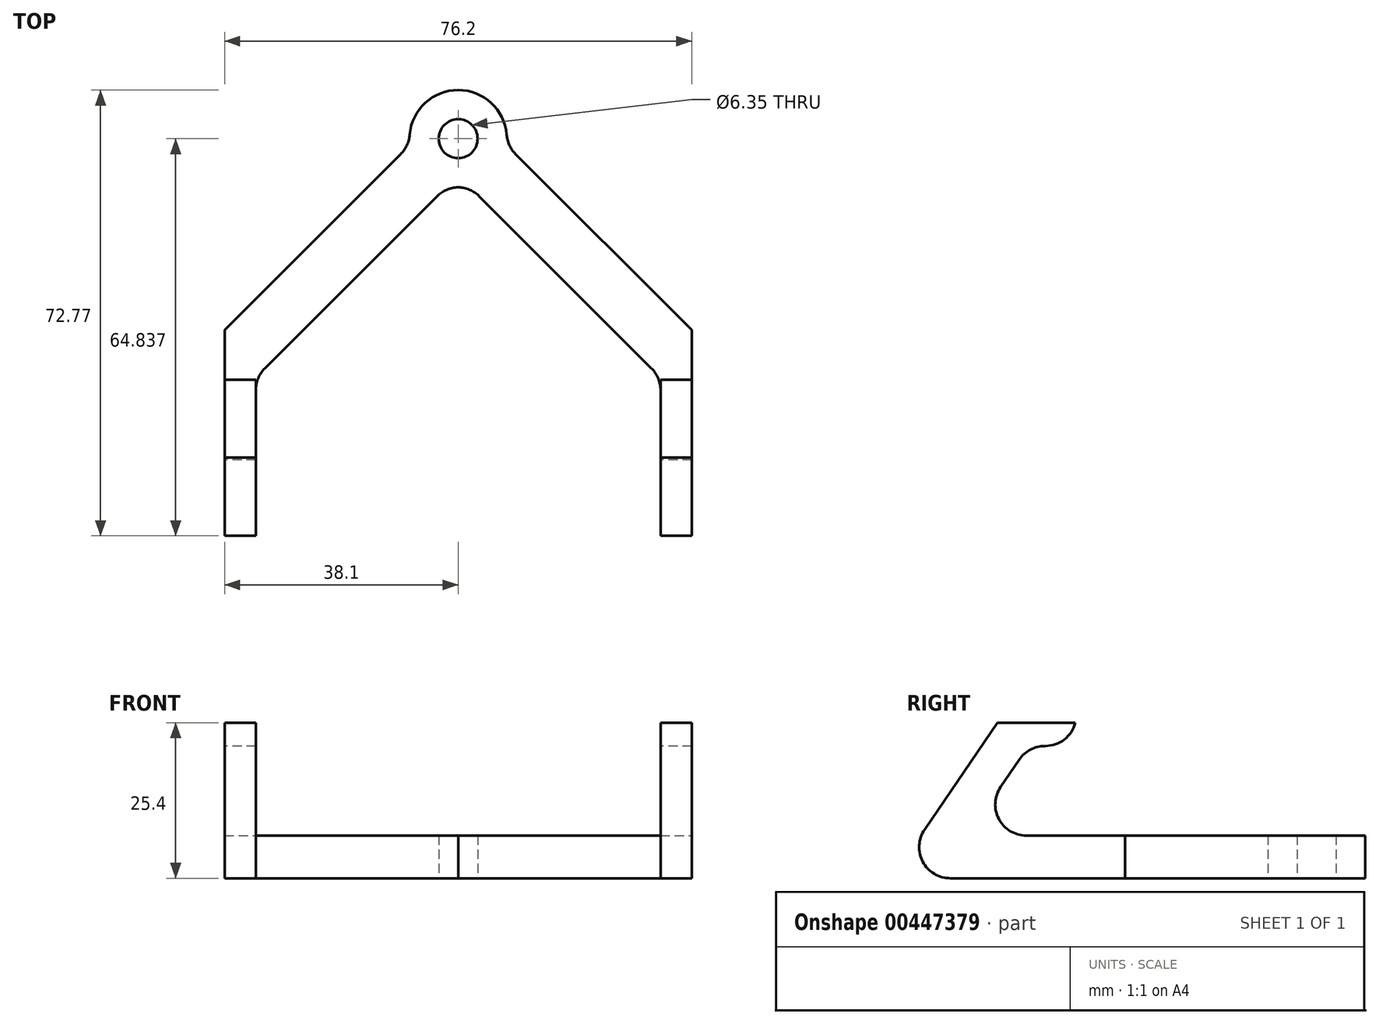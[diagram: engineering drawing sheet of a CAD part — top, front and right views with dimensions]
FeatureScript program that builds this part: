
annotation { "Feature Type Name" : "Feature", "Feature Type Description" : "" }
export const myFeature = defineFeature(function(context is Context, id is Id, definition is map)
    precondition{}
    {
        {
            var Q0;
            Q0=qCreatedBy(makeId("Top.planeOp"),FACE);
            var sketch = newSketch(context, id + "F0", { "sketchPlane" : qUnion([Q0])});
            skLineSegment(sketch, "E0.bottom", {"start": v(38.1, -38.1) * mm, "end": v(-38.1, -38.1) * mm});
            skLineSegment(sketch, "E0.top", {"start": v(38.1, 38.1) * mm, "end": v(-38.1, 38.1) * mm});
            skLineSegment(sketch, "E0.left", {"start": v(38.1, -38.1) * mm, "end": v(38.1, 38.1) * mm});
            skLineSegment(sketch, "E0.right", {"start": v(-38.1, -38.1) * mm, "end": v(-38.1, 38.1) * mm});
            skPoint(sketch, "E0.middle", {"position": v(0, 0) * mm});
            skSolve(sketch);
        }
        {
            var Q0;
            Q0=makeQuery(id+"F0.imprint","IMPRINT",FACE,{"disambiguationData":[TD([[makeQuery(id+"F0.imprint","IMPRINT",EDGE,{"derivedFrom":sQuery(id+"F0.wireOp",EDGE,"E0.bottom")}),-1.0]])]});
            extrude(context, id + "F1", {"entities" : qUnion([Q0]), "depth" : 25.4 * mm});
        }
        {
            var Q0;
            Q0=qCreatedBy(makeId("Right.planeOp"),FACE);
            var sketch = newSketch(context, id + "F2", { "sketchPlane" : qUnion([Q0])});
            skLineSegment(sketch, "E1.0.1", {"start": v(-38.1, 0) * mm, "end": v(-38.1, 25.4) * mm});
            skLineSegment(sketch, "E1.0.2", {"start": v(-38.1, 25.4) * mm, "end": v(-20.84, 25.4) * mm});
            skLineSegment(sketch, "E1.0.3", {"start": v(38.1, 25.4) * mm, "end": v(38.1, 6.96) * mm});
            skLineSegment(sketch, "E2", {"start": v(-8.1, 25.4) * mm, "end": v(-8.1, 21.59) * mm});
            skLineSegment(sketch, "E3", {"start": v(-8.1, 21.59) * mm, "end": v(-15.75, 21.59) * mm});
            skLineSegment(sketch, "E4", {"start": v(-15.75, 21.6) * mm, "end": v(-25.7, 6.96) * mm});
            skPoint(sketch, "E5.orphan", {"position": v(-30.42, 0) * mm});
            skLineSegment(sketch, "E6", {"start": v(-25.7, 6.96) * mm, "end": v(38.1, 6.96) * mm});
            skLineSegment(sketch, "E7", {"start": v(-20.84, 25.4) * mm, "end": v(-38.1, 0) * mm});
            skPoint(sketch, "E8.orphan", {"position": v(38.1, 0) * mm});
            skLineSegment(sketch, "E9.trimOffspring", {"start": v(-8.1, 25.4) * mm, "end": v(38.1, 25.4) * mm});
            skSolve(sketch);
        }
        {
            var Q0;
            Q0 = qSketchRegion(id + "F2", true);
            extrude(context, id + "F3", {"entities" : qUnion([Q0]), "operationType" : NewBodyOperationType.REMOVE, "endBound" : BoundingType.SYMMETRIC, "oppositeDirection" : true, "depth" : 76.2 * mm});
        }
        {
            var Q0;
            Q0=qCreatedBy(makeId("Top.planeOp"),FACE);
            var sketch = newSketch(context, id + "F4", { "sketchPlane" : qUnion([Q0])});
            skLineSegment(sketch, "E10.0.0", {"start": v(38.1, 0) * mm, "end": v(38.1, 38.1) * mm});
            skLineSegment(sketch, "E10.0.1", {"start": v(38.1, 38.1) * mm, "end": v(-38.1, 38.1) * mm});
            skLineSegment(sketch, "E10.0.2", {"start": v(-38.1, 38.1) * mm, "end": v(-38.1, 0) * mm});
            skLineSegment(sketch, "E10.0.3", {"start": v(-33.02, -38.1) * mm, "end": v(33.02, -38.1) * mm});
            skLineSegment(sketch, "E11.0.1", {"start": v(38.1, 38.1) * mm, "end": v(0, 38.1) * mm});
            skLineSegment(sketch, "E12", {"start": v(33.02, -38.1) * mm, "end": v(33.02, -7.73) * mm});
            skLineSegment(sketch, "E13", {"start": v(33.02, -7.73) * mm, "end": v(0, 25.3) * mm});
            skLineSegment(sketch, "E14", {"start": v(38.1, 0) * mm, "end": v(0, 38.1) * mm});
            skLineSegment(sketch, "E15.MirrorCS", {"start": v(-38.1, 0) * mm, "end": v(-38.1, 38.1) * mm});
            skLineSegment(sketch, "E16.MirrorCS", {"start": v(-33.02, -38.1) * mm, "end": v(-33.02, -7.73) * mm});
            skLineSegment(sketch, "E17.MirrorCS", {"start": v(-33.02, -7.73) * mm, "end": v(0, 25.3) * mm});
            skLineSegment(sketch, "E18.MirrorCS", {"start": v(-38.1, 0) * mm, "end": v(0, 38.1) * mm});
            skLineSegment(sketch, "E19", {"start": v(33.02, -38.1) * mm, "end": v(-33.02, -38.1) * mm});
            skPoint(sketch, "E20.orphan", {"position": v(38.1, -38.1) * mm});
            skPoint(sketch, "E21.orphan", {"position": v(-38.1, -38.1) * mm});
            skSolve(sketch);
        }
        {
            var Q0;
            Q0 = qSketchRegion(id + "F4", true);
            extrude(context, id + "F5", {"entities" : qUnion([Q0]), "operationType" : NewBodyOperationType.REMOVE, "endBound" : BoundingType.THROUGH_ALL, "depth" : 25.4 * mm});
        }
        {
            var Q0;
            Q0=makeQuery(id+"F0.imprint","IMPRINT",FACE,{"disambiguationData":[TD([[makeQuery(id+"F0.imprint","IMPRINT",EDGE,{"derivedFrom":sQuery(id+"F0.wireOp",EDGE,"E0.bottom")}),-1.0]])]});
            var sketch = newSketch(context, id + "F6", { "sketchPlane" : qUnion([Q0])});
            skCircle(sketch, "E22", {"center": v(0, 31.25) * mm, "radius": 7.94 * mm});
            skCircle(sketch, "E23", {"center": v(0, 31.25) * mm, "radius": 3.18 * mm});
            skSolve(sketch);
        }
        {
            var Q0;
            Q0=makeQuery(id+"F6.imprint","IMPRINT",FACE,{"disambiguationData":[TD([[makeQuery(id+"F6.imprint","IMPRINT",EDGE,{"derivedFrom":sQuery(id+"F6.wireOp",EDGE,"E23")}),-1.0]])]});
            var Q1;
            {var subQ0=sQuery(id+"F6.wireOp",EDGE,"E22");var subQ1=makeQuery(id+"F0.imprint","IMPRINT",EDGE,{"derivedFrom":sQuery(id+"F0.wireOp",EDGE,"E0.top")});var subQ2=makeQuery(id+"F6.imprint","INTERSECT",VERTEX,{"disambiguationData":[OD(0.0)],"derivedFrom":[subQ1,subQ0]});Q1=makeQuery(id+"F6.imprint","IMPRINT",FACE,{"disambiguationData":[TD([[makeQuery(id+"F6.imprint","IMPRINT",EDGE,{"disambiguationData":[TD([[subQ2,-1.0]])],"derivedFrom":subQ0}),1.0]])]});}
            var Q2;
            Q2=makeQuery(id+"F3.boolean.opBoolean","COPY",FACE,{"derivedFrom":makeQuery(id+"F3.opExtrude","SWEPT_FACE",FACE,{"disambiguationData":[OSD([sQuery(id+"F2.wireOp",EDGE,"E6")])]})});
            extrude(context, id + "F7", {"entities" : qUnion([Q0, Q1]), "operationType" : NewBodyOperationType.ADD, "endBound" : BoundingType.UP_TO_SURFACE, "endBoundEntityFace" : qUnion([Q2]), "depth" : 25.4 * mm});
        }
        {
            var Q0;
            Q0=makeQuery(id+"F6.imprint","IMPRINT",FACE,{"disambiguationData":[TD([[makeQuery(id+"F6.imprint","IMPRINT",EDGE,{"derivedFrom":sQuery(id+"F6.wireOp",EDGE,"E23")}),1.0]])]});
            extrude(context, id + "F8", {"entities" : qUnion([Q0]), "operationType" : NewBodyOperationType.REMOVE, "depth" : 25.4 * mm});
        }
        {
            var Q0;
            {var subQ0=sQuery(id+"F2.wireOp",EDGE,"E4");var subQ1=sQuery(id+"F2.wireOp",EDGE,"E6");Q0=makeQuery(id+"F5.boolean.opBoolean","SPLIT",EDGE,{"disambiguationData":[TD([makeQuery(id+"F1.opExtrude","SWEPT_FACE",FACE,{"disambiguationData":[OSD([sQuery(id+"F0.wireOp",EDGE,"E0.right")])]})])],"derivedFrom":makeQuery(id+"F3.boolean.opBoolean","COPY",EDGE,{"derivedFrom":makeQuery(id+"F3.opExtrude","SWEPT_EDGE",EDGE,{"disambiguationData":[OSD([subQ0,subQ1])]})})});}
            var Q1;
            Q1=makeQuery(id+"F5.boolean.opBoolean","COPY",EDGE,{"derivedFrom":makeQuery(id+"F5.opExtrude","SWEPT_EDGE",EDGE,{"disambiguationData":[OSD([sQuery(id+"F4.wireOp",EDGE,"E16.MirrorCS"),sQuery(id+"F4.wireOp",EDGE,"E17.MirrorCS")])]})});
            var Q2;
            Q2=makeQuery(id+"F5.boolean.opBoolean","COPY",EDGE,{"derivedFrom":makeQuery(id+"F5.opExtrude","SWEPT_EDGE",EDGE,{"disambiguationData":[OSD([sQuery(id+"F4.wireOp",EDGE,"E15.MirrorCS"),sQuery(id+"F4.wireOp",EDGE,"E18.MirrorCS")])]})});
            var Q3;
            Q3=makeQuery(id+"F5.boolean.opBoolean","COPY",EDGE,{"derivedFrom":makeQuery(id+"F5.opExtrude","SWEPT_EDGE",EDGE,{"disambiguationData":[OSD([sQuery(id+"F4.wireOp",EDGE,"E12"),sQuery(id+"F4.wireOp",EDGE,"E13")])]})});
            var Q4;
            Q4=makeQuery(id+"F5.boolean.opBoolean","COPY",EDGE,{"derivedFrom":makeQuery(id+"F5.opExtrude","SWEPT_EDGE",EDGE,{"disambiguationData":[OSD([sQuery(id+"F4.wireOp",EDGE,"E10.0.0"),sQuery(id+"F4.wireOp",EDGE,"E14")])]})});
            var Q5;
            {var subQ0=sQuery(id+"F2.wireOp",EDGE,"E4");var subQ1=sQuery(id+"F2.wireOp",EDGE,"E6");Q5=makeQuery(id+"F5.boolean.opBoolean","SPLIT",EDGE,{"disambiguationData":[TD([makeQuery(id+"F1.opExtrude","SWEPT_FACE",FACE,{"disambiguationData":[OSD([sQuery(id+"F0.wireOp",EDGE,"E0.left")])]})])],"derivedFrom":makeQuery(id+"F3.boolean.opBoolean","COPY",EDGE,{"derivedFrom":makeQuery(id+"F3.opExtrude","SWEPT_EDGE",EDGE,{"disambiguationData":[OSD([subQ0,subQ1])]})})});}
            fillet(context, id + "F9", {"entities" : qUnion([Q0, Q1, Q2, Q3, Q4, Q5]), "radius" : 5.08 * mm, "tangentPropagation" : true, "allowEdgeOverflow" : false});
        }
        {
            var Q0;
            {var subQ0=sQuery(id+"F0.wireOp",EDGE,"E0.left");var subQ1=sQuery(id+"F0.wireOp",EDGE,"E0.bottom");var subQ2=sQuery(id+"F2.wireOp",EDGE,"E7");Q0=makeQuery(id+"F5.boolean.opBoolean","SPLIT",EDGE,{"disambiguationData":[TD([makeQuery(id+"F1.opExtrude","SWEPT_FACE",FACE,{"disambiguationData":[OSD([subQ0])]})])],"derivedFrom":makeQuery(id+"F3.boolean.opBoolean","MERGE",EDGE,{"derivedFrom":[makeQuery(id+"F1.opExtrude","CAP_EDGE",EDGE,{"disambiguationData":[OSD([subQ1])],"isStart":true}),makeQuery(id+"F3.opExtrude","SWEPT_EDGE",EDGE,{"disambiguationData":[OSD([sQuery(id+"F2.wireOp",EDGE,"E1.0.1"),subQ2])]})]})});}
            var Q1;
            {var subQ0=sQuery(id+"F0.wireOp",EDGE,"E0.right");var subQ1=sQuery(id+"F0.wireOp",EDGE,"E0.bottom");var subQ2=sQuery(id+"F2.wireOp",EDGE,"E7");Q1=makeQuery(id+"F5.boolean.opBoolean","SPLIT",EDGE,{"disambiguationData":[TD([makeQuery(id+"F1.opExtrude","SWEPT_FACE",FACE,{"disambiguationData":[OSD([subQ0])]})])],"derivedFrom":makeQuery(id+"F3.boolean.opBoolean","MERGE",EDGE,{"derivedFrom":[makeQuery(id+"F1.opExtrude","CAP_EDGE",EDGE,{"disambiguationData":[OSD([subQ1])],"isStart":true}),makeQuery(id+"F3.opExtrude","SWEPT_EDGE",EDGE,{"disambiguationData":[OSD([sQuery(id+"F2.wireOp",EDGE,"E1.0.1"),subQ2])]})]})});}
            var Q2;
            Q2=makeQuery(id+"F7.boolean.opBoolean","INTERSECT",EDGE,{"derivedFrom":[makeQuery(id+"F5.boolean.opBoolean","COPY",FACE,{"derivedFrom":makeQuery(id+"F5.opExtrude","SWEPT_FACE",FACE,{"disambiguationData":[OSD([sQuery(id+"F4.wireOp",EDGE,"E14")])]})}),makeQuery(id+"F7.opExtrude","SWEPT_FACE",FACE,{"disambiguationData":[OSD([sQuery(id+"F6.wireOp",EDGE,"E22")])]})]});
            var Q3;
            Q3=makeQuery(id+"F7.boolean.opBoolean","INTERSECT",EDGE,{"derivedFrom":[makeQuery(id+"F5.boolean.opBoolean","COPY",FACE,{"derivedFrom":makeQuery(id+"F5.opExtrude","SWEPT_FACE",FACE,{"disambiguationData":[OSD([sQuery(id+"F4.wireOp",EDGE,"E18.MirrorCS")])]})}),makeQuery(id+"F7.opExtrude","SWEPT_FACE",FACE,{"disambiguationData":[OSD([sQuery(id+"F6.wireOp",EDGE,"E22")])]})]});
            var Q4;
            Q4=makeQuery(id+"F7.boolean.opBoolean","INTERSECT",EDGE,{"derivedFrom":[makeQuery(id+"F5.boolean.opBoolean","COPY",FACE,{"derivedFrom":makeQuery(id+"F5.opExtrude","SWEPT_FACE",FACE,{"disambiguationData":[OSD([sQuery(id+"F4.wireOp",EDGE,"E17.MirrorCS")])]})}),makeQuery(id+"F7.opExtrude","SWEPT_FACE",FACE,{"disambiguationData":[OSD([sQuery(id+"F6.wireOp",EDGE,"E22")])]})]});
            var Q5;
            Q5=makeQuery(id+"F7.boolean.opBoolean","INTERSECT",EDGE,{"derivedFrom":[makeQuery(id+"F5.boolean.opBoolean","COPY",FACE,{"derivedFrom":makeQuery(id+"F5.opExtrude","SWEPT_FACE",FACE,{"disambiguationData":[OSD([sQuery(id+"F4.wireOp",EDGE,"E13")])]})}),makeQuery(id+"F7.opExtrude","SWEPT_FACE",FACE,{"disambiguationData":[OSD([sQuery(id+"F6.wireOp",EDGE,"E22")])]})]});
            var Q6;
            {var subQ0=sQuery(id+"F0.wireOp",EDGE,"E0.left");var subQ1=sQuery(id+"F2.wireOp",EDGE,"E7");Q6=makeQuery(id+"F5.boolean.opBoolean","SPLIT",EDGE,{"disambiguationData":[TD([makeQuery(id+"F1.opExtrude","SWEPT_FACE",FACE,{"disambiguationData":[OSD([subQ0])]})])],"derivedFrom":makeQuery(id+"F3.boolean.opBoolean","COPY",EDGE,{"derivedFrom":makeQuery(id+"F3.opExtrude","SWEPT_EDGE",EDGE,{"disambiguationData":[OSD([sQuery(id+"F2.wireOp",EDGE,"E1.0.2"),subQ1])]})})});}
            var Q7;
            {var subQ0=sQuery(id+"F0.wireOp",EDGE,"E0.right");var subQ1=sQuery(id+"F2.wireOp",EDGE,"E7");Q7=makeQuery(id+"F5.boolean.opBoolean","SPLIT",EDGE,{"disambiguationData":[TD([makeQuery(id+"F1.opExtrude","SWEPT_FACE",FACE,{"disambiguationData":[OSD([subQ0])]})])],"derivedFrom":makeQuery(id+"F3.boolean.opBoolean","COPY",EDGE,{"derivedFrom":makeQuery(id+"F3.opExtrude","SWEPT_EDGE",EDGE,{"disambiguationData":[OSD([sQuery(id+"F2.wireOp",EDGE,"E1.0.2"),subQ1])]})})});}
            var Q8;
            {var subQ0=sQuery(id+"F2.wireOp",EDGE,"E3");var subQ1=sQuery(id+"F2.wireOp",EDGE,"E4");Q8=makeQuery(id+"F5.boolean.opBoolean","SPLIT",EDGE,{"disambiguationData":[TD([makeQuery(id+"F1.opExtrude","SWEPT_FACE",FACE,{"disambiguationData":[OSD([sQuery(id+"F0.wireOp",EDGE,"E0.left")])]})])],"derivedFrom":makeQuery(id+"F3.boolean.opBoolean","COPY",EDGE,{"derivedFrom":makeQuery(id+"F3.opExtrude","SWEPT_EDGE",EDGE,{"disambiguationData":[OSD([subQ0,subQ1])]})})});}
            var Q9;
            {var subQ0=sQuery(id+"F2.wireOp",EDGE,"E3");var subQ1=sQuery(id+"F2.wireOp",EDGE,"E4");Q9=makeQuery(id+"F5.boolean.opBoolean","SPLIT",EDGE,{"disambiguationData":[TD([makeQuery(id+"F1.opExtrude","SWEPT_FACE",FACE,{"disambiguationData":[OSD([sQuery(id+"F0.wireOp",EDGE,"E0.right")])]})])],"derivedFrom":makeQuery(id+"F3.boolean.opBoolean","COPY",EDGE,{"derivedFrom":makeQuery(id+"F3.opExtrude","SWEPT_EDGE",EDGE,{"disambiguationData":[OSD([subQ0,subQ1])]})})});}
            var Q10;
            {var subQ0=sQuery(id+"F2.wireOp",EDGE,"E2");var subQ1=sQuery(id+"F2.wireOp",EDGE,"E3");Q10=makeQuery(id+"F5.boolean.opBoolean","SPLIT",EDGE,{"disambiguationData":[TD([makeQuery(id+"F1.opExtrude","SWEPT_FACE",FACE,{"disambiguationData":[OSD([sQuery(id+"F0.wireOp",EDGE,"E0.left")])]})])],"derivedFrom":makeQuery(id+"F3.boolean.opBoolean","COPY",EDGE,{"derivedFrom":makeQuery(id+"F3.opExtrude","SWEPT_EDGE",EDGE,{"disambiguationData":[OSD([subQ0,subQ1])]})})});}
            var Q11;
            {var subQ0=sQuery(id+"F2.wireOp",EDGE,"E3");var subQ1=sQuery(id+"F2.wireOp",EDGE,"E2");Q11=makeQuery(id+"F5.boolean.opBoolean","SPLIT",EDGE,{"disambiguationData":[TD([makeQuery(id+"F1.opExtrude","SWEPT_FACE",FACE,{"disambiguationData":[OSD([sQuery(id+"F0.wireOp",EDGE,"E0.right")])]})])],"derivedFrom":makeQuery(id+"F3.boolean.opBoolean","COPY",EDGE,{"derivedFrom":makeQuery(id+"F3.opExtrude","SWEPT_EDGE",EDGE,{"disambiguationData":[OSD([subQ1,subQ0])]})})});}
            fillet(context, id + "F10", {"entities" : qUnion([Q0, Q1, Q2, Q3, Q4, Q5, Q6, Q7, Q8, Q9, Q10, Q11]), "radius" : 5.08 * mm, "tangentPropagation" : true, "allowEdgeOverflow" : false});
        }
    });
